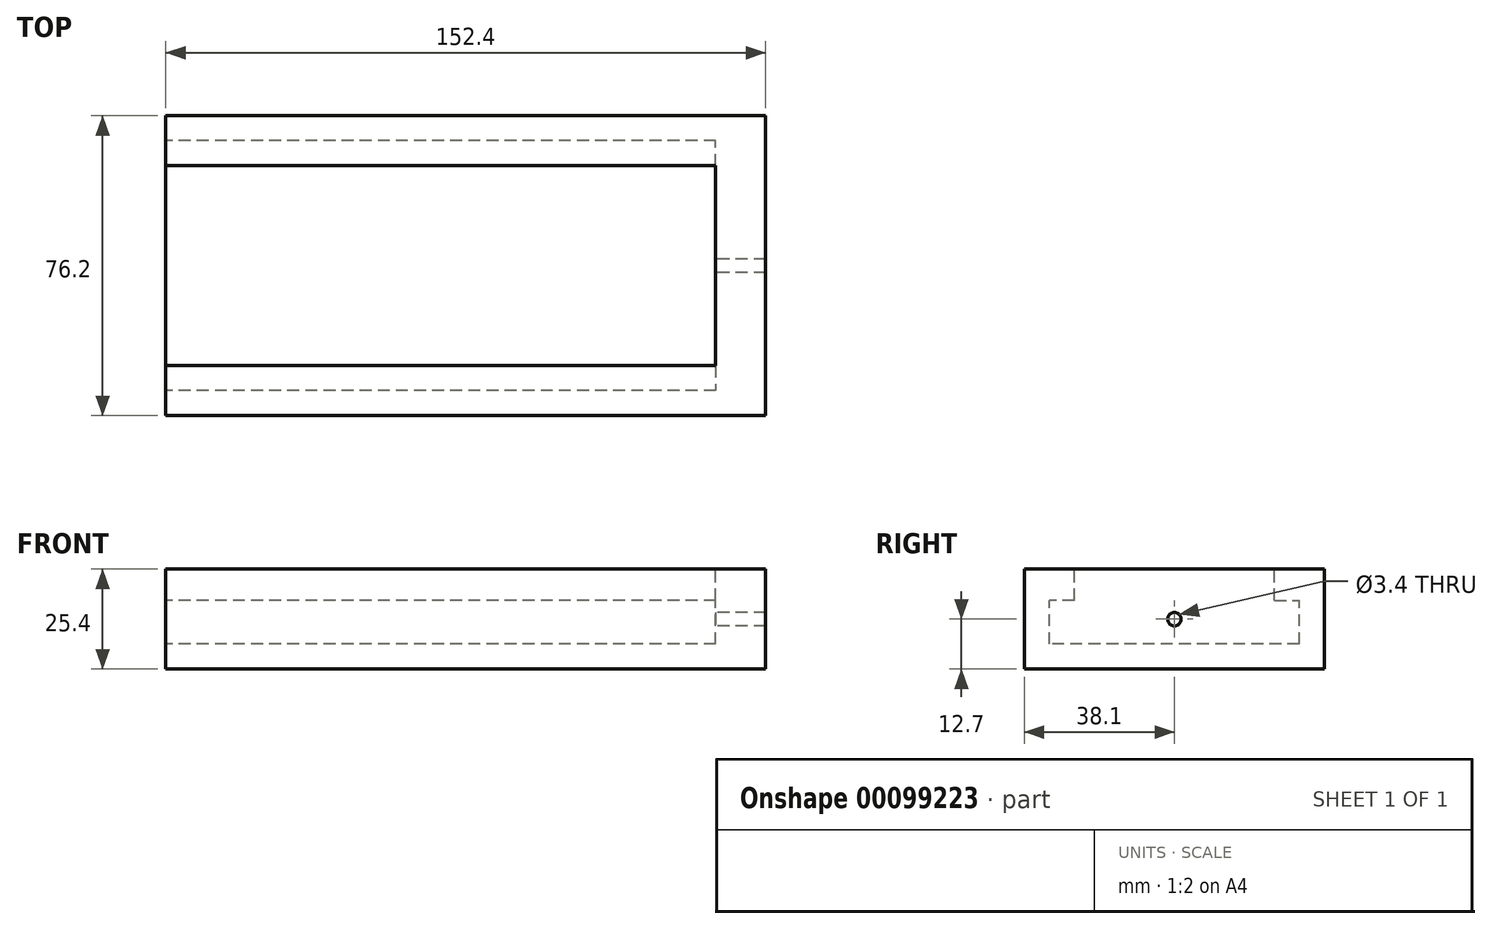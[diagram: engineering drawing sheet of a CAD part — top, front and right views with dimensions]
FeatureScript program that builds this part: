
annotation { "Feature Type Name" : "Feature", "Feature Type Description" : "" }
export const myFeature = defineFeature(function(context is Context, id is Id, definition is map)
    precondition{}
    {
        {
            var Q0;
            Q0=qCreatedBy(makeId("Top.planeOp"),FACE);
            var sketch = newSketch(context, id + "F0", { "sketchPlane" : qUnion([Q0])});
            skLineSegment(sketch, "E0.bottom", {"start": v(76.2, 38.1) * mm, "end": v(-76.2, 38.1) * mm});
            skLineSegment(sketch, "E0.top", {"start": v(76.2, -38.1) * mm, "end": v(-76.2, -38.1) * mm});
            skLineSegment(sketch, "E0.left", {"start": v(76.2, 38.1) * mm, "end": v(76.2, -38.1) * mm});
            skLineSegment(sketch, "E0.right", {"start": v(-76.2, 38.1) * mm, "end": v(-76.2, -38.1) * mm});
            skPoint(sketch, "E0.middle", {"position": v(0, 0) * mm});
            skSolve(sketch);
        }
        {
            var Q0;
            Q0 = qSketchRegion(id + "F0", true);
            extrude(context, id + "F1", {"entities" : qUnion([Q0]), "depth" : 25.4 * mm});
        }
        {
            var Q0;
            Q0=makeQuery(id+"F1.opExtrude","CAP_FACE",FACE,{"disambiguationData":[OSD([sQuery(id+"F0.wireOp",EDGE,"E0.bottom"),sQuery(id+"F0.wireOp",EDGE,"E0.top"),sQuery(id+"F0.wireOp",EDGE,"E0.left"),sQuery(id+"F0.wireOp",EDGE,"E0.right")])],"isStart":false});
            var sketch = newSketch(context, id + "F2", { "sketchPlane" : qUnion([Q0])});
            skLineSegment(sketch, "E1.bottom", {"start": v(-76.2, 25.4) * mm, "end": v(63.5, 25.4) * mm});
            skLineSegment(sketch, "E1.top", {"start": v(-76.2, -25.4) * mm, "end": v(63.5, -25.4) * mm});
            skLineSegment(sketch, "E1.left", {"start": v(-76.2, 25.4) * mm, "end": v(-76.2, -25.4) * mm});
            skLineSegment(sketch, "E1.right", {"start": v(63.5, 25.4) * mm, "end": v(63.5, -25.4) * mm});
            skSolve(sketch);
        }
        {
            var Q0;
            Q0 = qSketchRegion(id + "F2", true);
            extrude(context, id + "F3", {"entities" : qUnion([Q0]), "operationType" : NewBodyOperationType.REMOVE, "oppositeDirection" : true, "depth" : 19.05 * mm});
        }
        {
            var Q0;
            Q0=makeQuery(id+"F1.opExtrude","SWEPT_FACE",FACE,{"disambiguationData":[OSD([sQuery(id+"F0.wireOp",EDGE,"E0.right")])]});
            var sketch = newSketch(context, id + "F4", { "sketchPlane" : qUnion([Q0])});
            skLineSegment(sketch, "E2.bottom", {"start": v(-25.4, 6.35) * mm, "end": v(-31.75, 6.35) * mm});
            skLineSegment(sketch, "E2.top", {"start": v(-25.4, 17.46) * mm, "end": v(-31.75, 17.46) * mm});
            skLineSegment(sketch, "E2.left", {"start": v(-25.4, 6.35) * mm, "end": v(-25.4, 17.46) * mm});
            skLineSegment(sketch, "E2.right", {"start": v(-31.75, 6.35) * mm, "end": v(-31.75, 17.46) * mm});
            skLineSegment(sketch, "E3.bottom", {"start": v(25.4, 6.35) * mm, "end": v(31.75, 6.35) * mm});
            skLineSegment(sketch, "E3.top", {"start": v(25.4, 17.46) * mm, "end": v(31.75, 17.46) * mm});
            skLineSegment(sketch, "E3.left", {"start": v(25.4, 6.35) * mm, "end": v(25.4, 17.46) * mm});
            skLineSegment(sketch, "E3.right", {"start": v(31.75, 6.35) * mm, "end": v(31.75, 17.46) * mm});
            skSolve(sketch);
        }
        {
            var Q0;
            Q0 = qSketchRegion(id + "F4", true);
            extrude(context, id + "F5", {"entities" : qUnion([Q0]), "operationType" : NewBodyOperationType.REMOVE, "oppositeDirection" : true, "depth" : 139.7 * mm});
        }
        {
            var Q0;
            Q0=makeQuery(id+"F5.boolean.opBoolean","MERGE",FACE,{"derivedFrom":[makeQuery(id+"F3.boolean.opBoolean","COPY",FACE,{"derivedFrom":makeQuery(id+"F3.opExtrude","SWEPT_FACE",FACE,{"disambiguationData":[OSD([sQuery(id+"F2.wireOp",EDGE,"E1.right")])]})}),makeQuery(id+"F5.opExtrude","CAP_FACE",FACE,{"disambiguationData":[OSD([sQuery(id+"F4.wireOp",EDGE,"E2.bottom"),sQuery(id+"F4.wireOp",EDGE,"E2.top"),sQuery(id+"F4.wireOp",EDGE,"E2.left"),sQuery(id+"F4.wireOp",EDGE,"E2.right")])],"isStart":false}),makeQuery(id+"F5.opExtrude","CAP_FACE",FACE,{"disambiguationData":[OSD([sQuery(id+"F4.wireOp",EDGE,"E3.bottom"),sQuery(id+"F4.wireOp",EDGE,"E3.top"),sQuery(id+"F4.wireOp",EDGE,"E3.left"),sQuery(id+"F4.wireOp",EDGE,"E3.right")])],"isStart":false})]});
            var sketch = newSketch(context, id + "F6", { "sketchPlane" : qUnion([Q0])});
            skCircle(sketch, "E4", {"center": v(0, 12.7) * mm, "radius": 1.7 * mm});
            skSolve(sketch);
        }
        {
            var Q0;
            Q0 = qSketchRegion(id + "F6", true);
            extrude(context, id + "F7", {"entities" : qUnion([Q0]), "operationType" : NewBodyOperationType.REMOVE, "oppositeDirection" : true, "depth" : 12.7 * mm});
        }
    });
